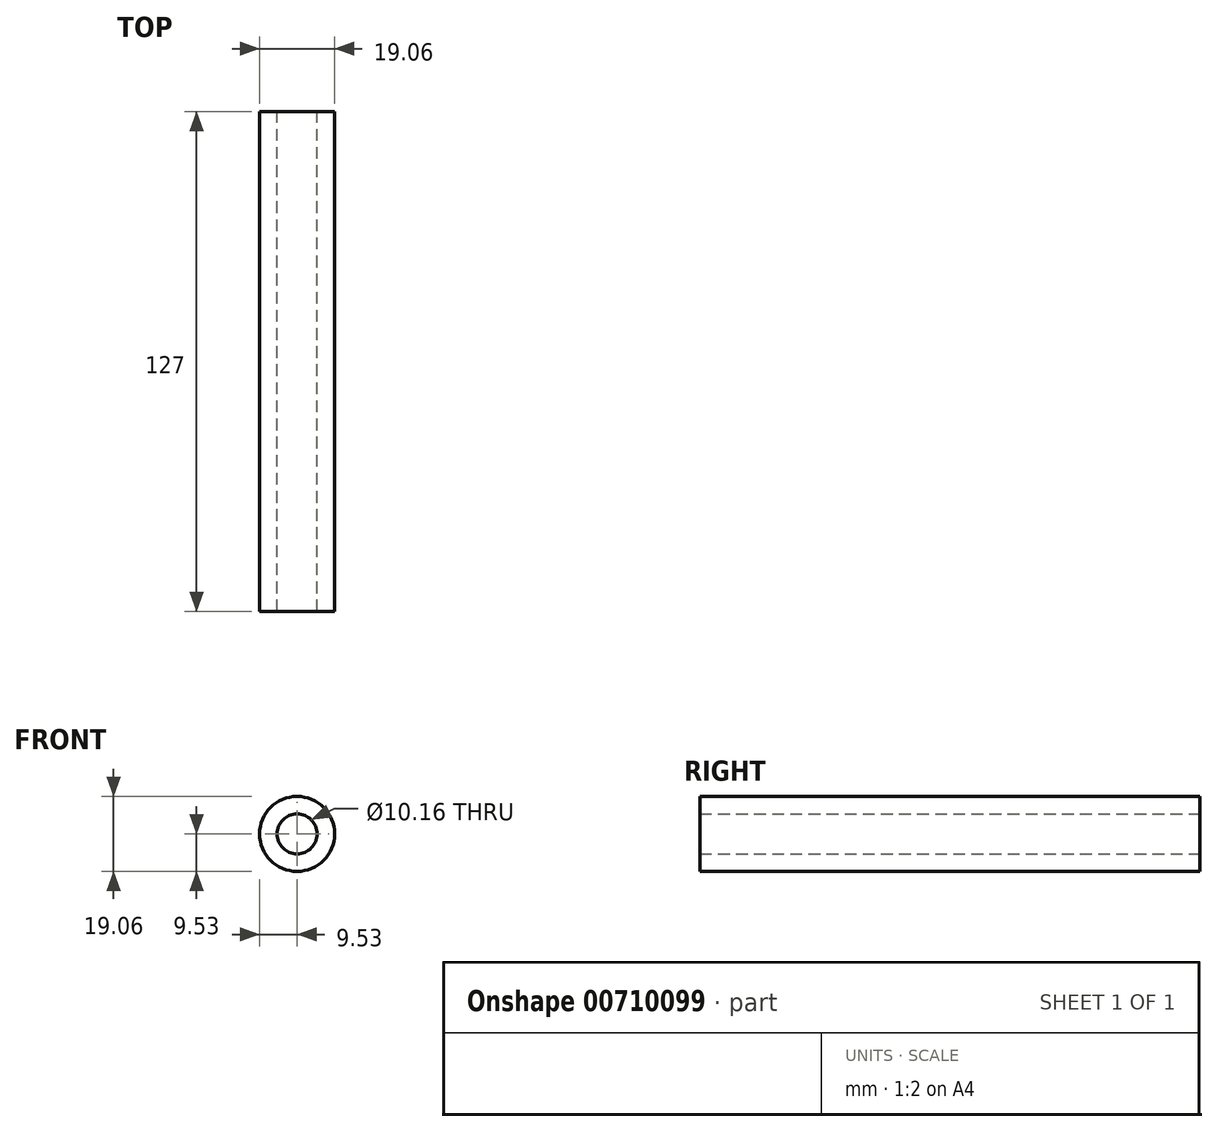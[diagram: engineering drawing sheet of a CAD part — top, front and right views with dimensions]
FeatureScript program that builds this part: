
annotation { "Feature Type Name" : "Feature", "Feature Type Description" : "" }
export const myFeature = defineFeature(function(context is Context, id is Id, definition is map)
    precondition{}
    {
        {
            var Q0;
            Q0=qCreatedBy(makeId("Front.planeOp"),FACE);
            var sketch = newSketch(context, id + "F0", { "sketchPlane" : qUnion([Q0])});
            skCircle(sketch, "E0", {"center": v(0, 0) * mm, "radius": 9.53 * mm});
            skCircle(sketch, "E1", {"center": v(0, 0) * mm, "radius": 5.08 * mm});
            skSolve(sketch);
        }
        {
            var Q0;
            Q0 = qSketchRegion(id + "F0", true);
            extrude(context, id + "F1", {"entities" : qUnion([Q0]), "endBound" : BoundingType.SYMMETRIC, "depth" : 127 * mm, "offsetDistance" : 25.4 * mm});
        }
    });
